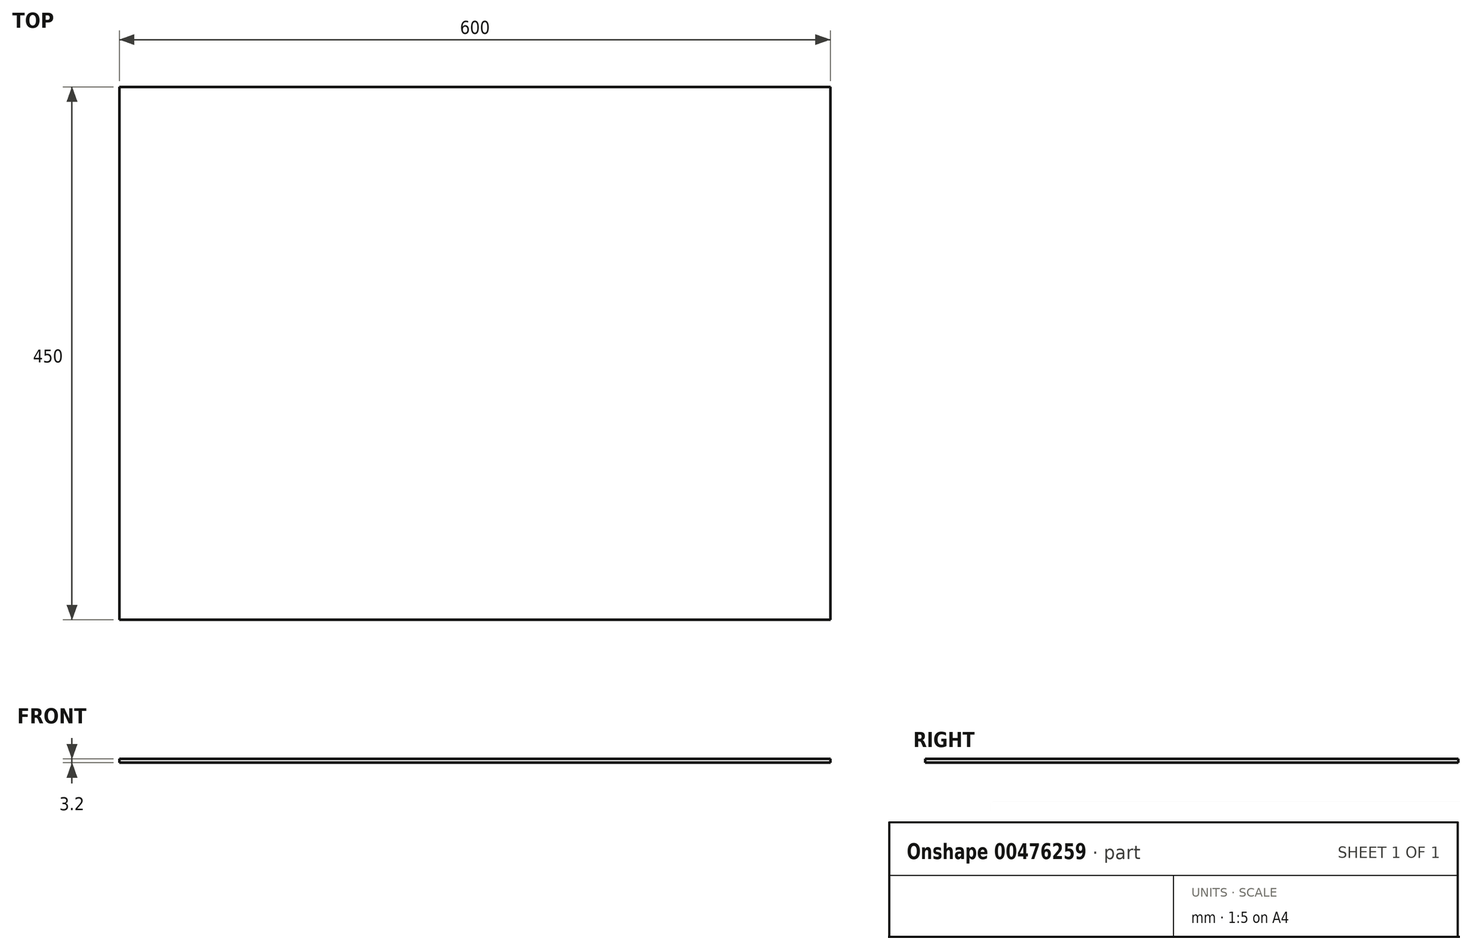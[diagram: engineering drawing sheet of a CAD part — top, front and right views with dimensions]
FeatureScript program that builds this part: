
annotation { "Feature Type Name" : "Feature", "Feature Type Description" : "" }
export const myFeature = defineFeature(function(context is Context, id is Id, definition is map)
    precondition{}
    {
        {
            var Q0;
            Q0=qCreatedBy(makeId("Top.planeOp"),FACE);
            var sketch = newSketch(context, id + "F0", { "sketchPlane" : qUnion([Q0])});
            skLineSegment(sketch, "E0.bottom", {"start": v(-317.86, 237.95) * mm, "end": v(282.14, 237.95) * mm});
            skLineSegment(sketch, "E0.top", {"start": v(-317.86, -212.05) * mm, "end": v(282.14, -212.05) * mm});
            skLineSegment(sketch, "E0.left", {"start": v(-317.86, 237.95) * mm, "end": v(-317.86, -212.05) * mm});
            skLineSegment(sketch, "E0.right", {"start": v(282.14, 237.95) * mm, "end": v(282.14, -212.05) * mm});
            skSolve(sketch);
        }
        {
            var Q0;
            Q0=makeQuery(id+"F0.imprint","IMPRINT",FACE,{"disambiguationData":[TD([[makeQuery(id+"F0.imprint","IMPRINT",EDGE,{"derivedFrom":sQuery(id+"F0.wireOp",EDGE,"E0.bottom")}),-1.0]])]});
            extrude(context, id + "F1", {"entities" : qUnion([Q0]), "depth" : 3.2 * mm, "offsetDistance" : 25 * mm});
        }
    });
